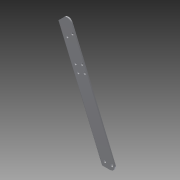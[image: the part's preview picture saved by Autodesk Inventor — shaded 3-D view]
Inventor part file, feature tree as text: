
AUTODESK INVENTOR PART (.ipt)
format: ipt  version: 2014 SP1 (Build 180222100, 222)  size: 162,304 bytes
history: native  units: in
note: dims shown in document units (in); Inventor stores cm internally (conversion verified against a paired STEP export)
features: other x3, sketch x1
ambient origin geometry x8: Origin, YZ Plane, XZ Plane, XY Plane, X Axis, Y Axis, Z Axis, Center Point
bodies: Solid1 (feature_tree)
feature tree (4):
  other  "V5 Shooter Frame Side Connector P3.ipt"
  other  "Solid1::V5 Shooter Frame Side Connector P3.ipt"
  sketch  "Sketch1"  dims[d0=0.3937in]
  other  "TaggingFeature1"
